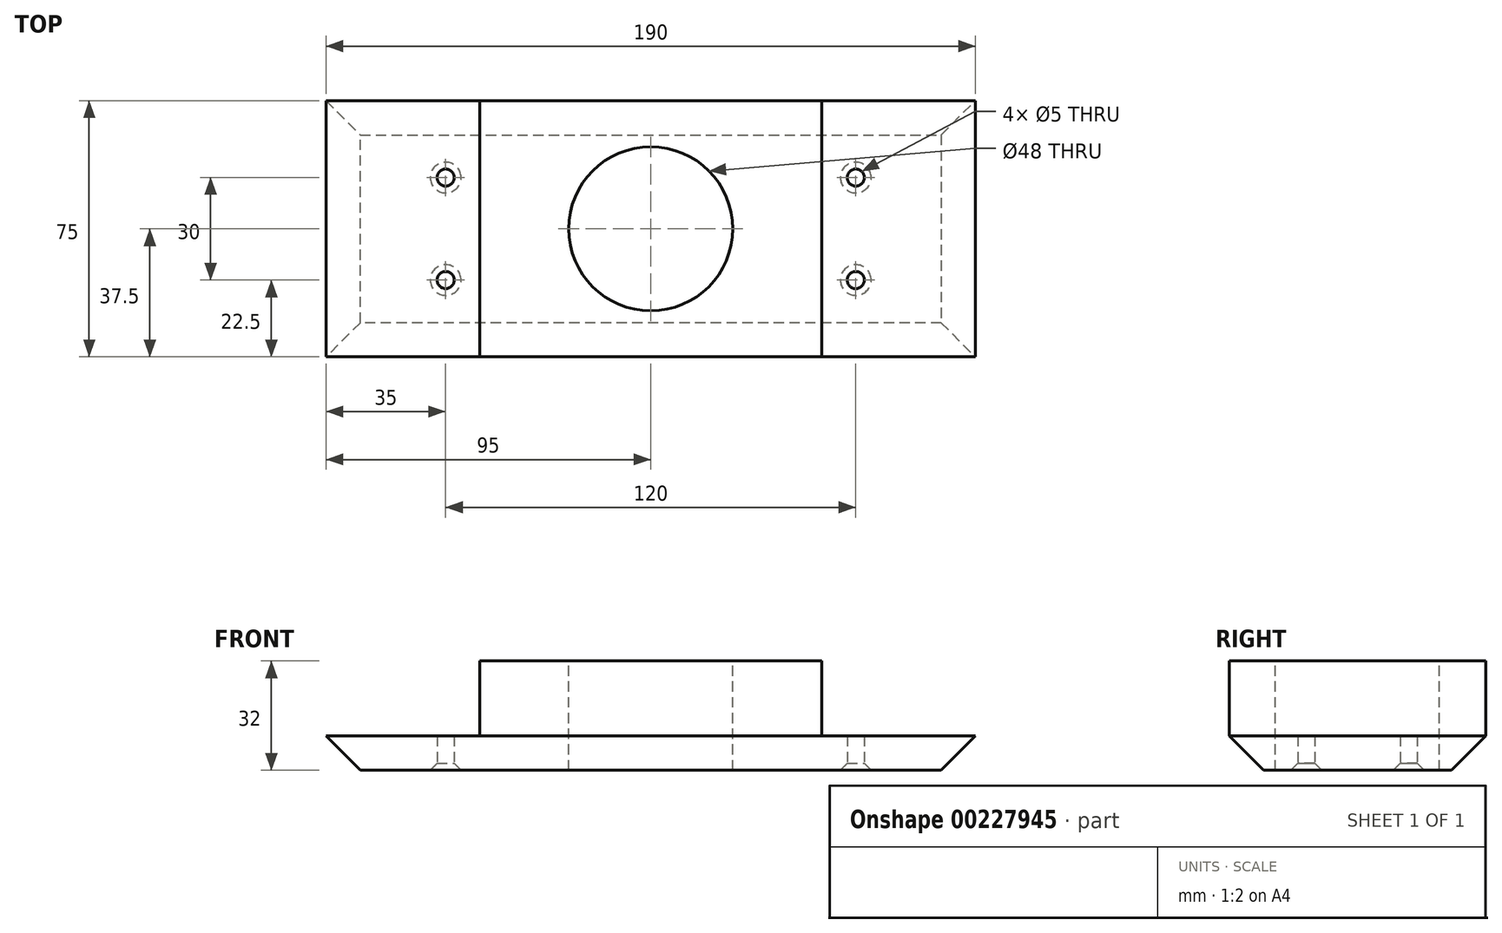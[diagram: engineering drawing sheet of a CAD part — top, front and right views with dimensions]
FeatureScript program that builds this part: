
annotation { "Feature Type Name" : "Feature", "Feature Type Description" : "" }
export const myFeature = defineFeature(function(context is Context, id is Id, definition is map)
    precondition{}
    {
        {
            var Q0;
            Q0=qCreatedBy(makeId("Top.planeOp"),FACE);
            var sketch = newSketch(context, id + "F0", { "sketchPlane" : qUnion([Q0])});
            skLineSegment(sketch, "E0.bottom", {"start": v(-95, 37.5) * mm, "end": v(95, 37.5) * mm});
            skLineSegment(sketch, "E0.top", {"start": v(-95, -37.5) * mm, "end": v(95, -37.5) * mm});
            skLineSegment(sketch, "E0.left", {"start": v(-95, 37.5) * mm, "end": v(-95, -37.5) * mm});
            skLineSegment(sketch, "E0.right", {"start": v(95, 37.5) * mm, "end": v(95, -37.5) * mm});
            skPoint(sketch, "E1", {"position": v(0, 37.5) * mm});
            skPoint(sketch, "E2", {"position": v(-95, 0) * mm});
            skSolve(sketch);
        }
        {
            var Q0;
            Q0=makeQuery(id+"F0.imprint","IMPRINT",FACE,{"disambiguationData":[TD([[makeQuery(id+"F0.imprint","IMPRINT",EDGE,{"derivedFrom":sQuery(id+"F0.wireOp",EDGE,"E0.bottom")}),-1.0]])]});
            extrude(context, id + "F1", {"entities" : qUnion([Q0]), "depth" : 10 * mm});
        }
        {
            var Q0;
            Q0=makeQuery(id+"F1.opExtrude","CAP_FACE",FACE,{"disambiguationData":[OSD([sQuery(id+"F0.wireOp",EDGE,"E0.bottom"),sQuery(id+"F0.wireOp",EDGE,"E0.top"),sQuery(id+"F0.wireOp",EDGE,"E0.left"),sQuery(id+"F0.wireOp",EDGE,"E0.right")])],"isStart":false});
            var sketch = newSketch(context, id + "F2", { "sketchPlane" : qUnion([Q0])});
            skLineSegment(sketch, "E3.bottom", {"start": v(50, 37.5) * mm, "end": v(-50, 37.5) * mm});
            skLineSegment(sketch, "E3.top", {"start": v(50, -37.5) * mm, "end": v(-50, -37.5) * mm});
            skLineSegment(sketch, "E3.left", {"start": v(50, 37.5) * mm, "end": v(50, -37.5) * mm});
            skLineSegment(sketch, "E3.right", {"start": v(-50, 37.5) * mm, "end": v(-50, -37.5) * mm});
            skPoint(sketch, "E4", {"position": v(0, 37.5) * mm});
            skSolve(sketch);
        }
        {
            var Q0;
            Q0=makeQuery(id+"F2.imprint","IMPRINT",FACE,{"disambiguationData":[TD([[makeQuery(id+"F2.imprint","IMPRINT",EDGE,{"derivedFrom":sQuery(id+"F2.wireOp",EDGE,"E3.bottom")}),-1.0]])]});
            extrude(context, id + "F3", {"entities" : qUnion([Q0]), "operationType" : NewBodyOperationType.ADD, "depth" : 22 * mm});
        }
        {
            var Q0;
            Q0=makeQuery(id+"F3.opExtrude","CAP_FACE",FACE,{"disambiguationData":[OSD([sQuery(id+"F2.wireOp",EDGE,"E3.bottom"),sQuery(id+"F2.wireOp",EDGE,"E3.top"),sQuery(id+"F2.wireOp",EDGE,"E3.left"),sQuery(id+"F2.wireOp",EDGE,"E3.right")])],"isStart":false});
            var sketch = newSketch(context, id + "F4", { "sketchPlane" : qUnion([Q0])});
            skCircle(sketch, "E5", {"center": v(0, 0) * mm, "radius": 24 * mm});
            skSolve(sketch);
        }
        {
            var Q0;
            Q0=makeQuery(id+"F4.imprint","IMPRINT",FACE,{"disambiguationData":[TD([[makeQuery(id+"F4.imprint","IMPRINT",EDGE,{"derivedFrom":sQuery(id+"F4.wireOp",EDGE,"E5")}),1.0]])]});
            extrude(context, id + "F5", {"entities" : qUnion([Q0]), "operationType" : NewBodyOperationType.REMOVE, "endBound" : BoundingType.THROUGH_ALL, "oppositeDirection" : true, "depth" : 25 * mm});
        }
        {
            var Q0;
            Q0=makeQuery(id+"F1.opExtrude","CAP_EDGE",EDGE,{"disambiguationData":[OSD([sQuery(id+"F0.wireOp",EDGE,"E0.right")])],"isStart":true});
            var Q1;
            Q1=makeQuery(id+"F1.opExtrude","CAP_EDGE",EDGE,{"disambiguationData":[OSD([sQuery(id+"F0.wireOp",EDGE,"E0.left")])],"isStart":true});
            var Q2;
            Q2=makeQuery(id+"F1.opExtrude","CAP_EDGE",EDGE,{"disambiguationData":[OSD([sQuery(id+"F0.wireOp",EDGE,"E0.bottom")])],"isStart":true});
            var Q3;
            Q3=makeQuery(id+"F1.opExtrude","CAP_EDGE",EDGE,{"disambiguationData":[OSD([sQuery(id+"F0.wireOp",EDGE,"E0.top")])],"isStart":true});
            chamfer(context, id + "F6", {"entities" : qUnion([Q0, Q1, Q2, Q3]), "width" : 10 * mm, "tangentPropagation" : true});
        }
        {
            var Q0;
            Q0=makeQuery(id+"F1.opExtrude","CAP_FACE",FACE,{"disambiguationData":[OSD([sQuery(id+"F0.wireOp",EDGE,"E0.bottom"),sQuery(id+"F0.wireOp",EDGE,"E0.top"),sQuery(id+"F0.wireOp",EDGE,"E0.left"),sQuery(id+"F0.wireOp",EDGE,"E0.right")])],"isStart":true});
            var sketch = newSketch(context, id + "F7", { "sketchPlane" : qUnion([Q0])});
            skPoint(sketch, "E6", {"position": v(-60, 15) * mm});
            skPoint(sketch, "E7.MirrorP", {"position": v(60, 15) * mm});
            skPoint(sketch, "E8.MirrorP", {"position": v(-60, -15) * mm});
            skPoint(sketch, "E9.MirrorP", {"position": v(60, -15) * mm});
            skSolve(sketch);
        }
        {
            var Q0;
            Q0=sQuery(id+"F7.wireOp",VERTEX,"E6");
            var Q1;
            Q1=sQuery(id+"F7.wireOp",VERTEX,"E8.MirrorP");
            var Q2;
            Q2=sQuery(id+"F7.wireOp",VERTEX,"E7.MirrorP");
            var Q3;
            Q3=sQuery(id+"F7.wireOp",VERTEX,"E9.MirrorP");
            var Q4;
            Q4=makeQuery(id+"F1.opExtrude","SWEPT_BODY",BODY,{"disambiguationData":[OSD([sQuery(id+"F0.wireOp",EDGE,"E0.bottom"),sQuery(id+"F0.wireOp",EDGE,"E0.top"),sQuery(id+"F0.wireOp",EDGE,"E0.left"),sQuery(id+"F0.wireOp",EDGE,"E0.right")])]});
            hole(context, id + "F8", {"style" : HoleStyle.C_SINK, "endStyle" : HoleEndStyle.THROUGH, "holeDiameter" : 5 * mm, "cSinkDiameter" : 9 * mm, "cSinkAngle" : 90 * degree, "locations" : qUnion([Q0, Q1, Q2, Q3]), "scope" : qUnion([Q4]), "isTappedThrough" : true});
        }
    });
